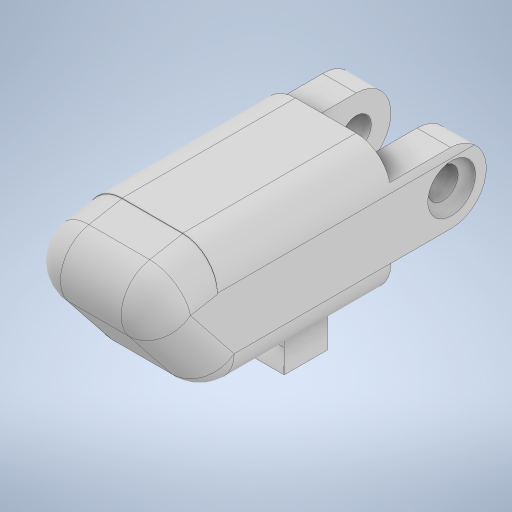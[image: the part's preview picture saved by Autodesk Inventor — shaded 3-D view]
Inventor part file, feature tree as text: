
AUTODESK INVENTOR PART (.ipt)
format: ipt  version: 2024 (Build 280153000, 153)  size: 359,936 bytes
history: native  units: mm
features: extrude x6, sketch x6, fillet x4, other x1
ambient origin geometry x8: Origin, YZ Plane, XZ Plane, XY Plane, X Axis, Y Axis, Z Axis, Center Point
bodies: Body1 (feature_tree), Body2 (feature_tree)
feature tree (17):
  other  "Твердое тело1"
  extrude  "Выдавливание1"  Depth=20.0mm
  extrude  "Выдавливание2"  Depth=15.0mm
  extrude  "Выдавливание3"  Depth=15.0mm TaperAngle=0.0deg
  extrude  "Выдавливание4"  Depth=8.0mm
  fillet  "Сопряжение1"  Radius=11.0mm
  fillet  "Сопряжение2"  Radius=3.0mm
  extrude  "Выдавливание5"  Depth=4.0mm
  extrude  "Выдавливание6"  Depth=4.0mm
  fillet  "Сопряжение3"  Radius=3.5mm
  fillet  "Сопряжение4"  Radius=15.0mm
  sketch  "Эскиз1"
  sketch  "Эскиз2"
  sketch  "Эскиз3"
  sketch  "Эскиз4"
  sketch  "Эскиз5"
  sketch  "Эскиз6"
